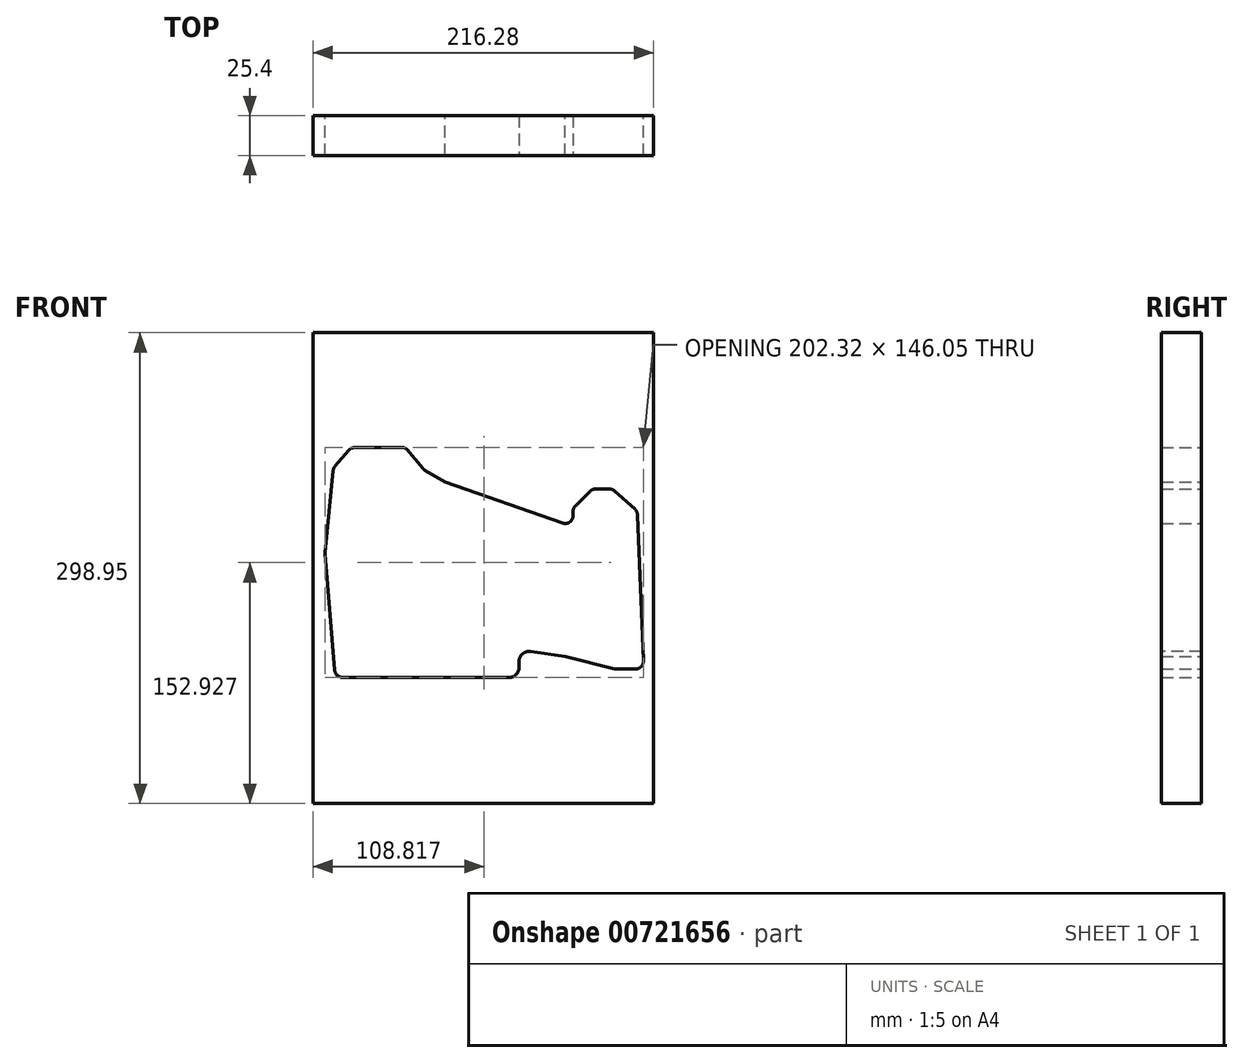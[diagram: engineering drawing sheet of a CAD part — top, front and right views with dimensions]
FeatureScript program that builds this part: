
annotation { "Feature Type Name" : "Feature", "Feature Type Description" : "" }
export const myFeature = defineFeature(function(context is Context, id is Id, definition is map)
    precondition{}
    {
        {
            var Q0;
            Q0=qCreatedBy(makeId("Front.planeOp"),FACE);
            var sketch = newSketch(context, id + "F0", { "sketchPlane" : qUnion([Q0])});
            skLineSegment(sketch, "E0", {"start": v(130.02, -238.75) * mm, "end": v(184.62, -238.75) * mm});
            skLineSegment(sketch, "E1", {"start": v(189.16, -236.13) * mm, "end": v(199.3, -218.55) * mm});
            skLineSegment(sketch, "E2", {"start": v(204.57, -215.98) * mm, "end": v(270.45, -225.26) * mm});
            skLineSegment(sketch, "E3", {"start": v(271, -225.37) * mm, "end": v(302.47, -233.24) * mm});
            skLineSegment(sketch, "E4", {"start": v(303.74, -233.4) * mm, "end": v(315.7, -233.4) * mm});
            skLineSegment(sketch, "E5", {"start": v(320.94, -227.94) * mm, "end": v(317.18, -135.48) * mm});
            skLineSegment(sketch, "E6", {"start": v(315.45, -131.79) * mm, "end": v(302.64, -120.31) * mm});
            skLineSegment(sketch, "E7", {"start": v(299.14, -118.98) * mm, "end": v(290.57, -118.98) * mm});
            skLineSegment(sketch, "E8", {"start": v(286.87, -120.51) * mm, "end": v(277.73, -129.65) * mm});
            skLineSegment(sketch, "E9", {"start": v(276.2, -133.35) * mm, "end": v(276.2, -160.7) * mm});
            skLineSegment(sketch, "E10", {"start": v(269.2, -165.64) * mm, "end": v(245.67, -157.25) * mm});
            skLineSegment(sketch, "E11", {"start": v(243.91, -156.95) * mm, "end": v(226.78, -156.95) * mm});
            skLineSegment(sketch, "E12", {"start": v(221.57, -152.22) * mm, "end": v(220.11, -137.37) * mm});
            skLineSegment(sketch, "E13", {"start": v(214.39, -132.66) * mm, "end": v(204.23, -133.66) * mm});
            skLineSegment(sketch, "E14", {"start": v(198.5, -128.95) * mm, "end": v(197.5, -118.56) * mm});
            skLineSegment(sketch, "E15", {"start": v(194.92, -114.55) * mm, "end": v(182.28, -107.17) * mm});
            skLineSegment(sketch, "E16", {"start": v(180.9, -106.01) * mm, "end": v(170.8, -93.97) * mm});
            skLineSegment(sketch, "E17", {"start": v(168.06, -92.7) * mm, "end": v(137.46, -92.7) * mm});
            skLineSegment(sketch, "E18", {"start": v(133.47, -94.54) * mm, "end": v(125.07, -104.4) * mm});
            skLineSegment(sketch, "E19", {"start": v(123.85, -107.27) * mm, "end": v(118.64, -159.2) * mm});
            skLineSegment(sketch, "E20", {"start": v(118.63, -160.17) * mm, "end": v(124.8, -233.94) * mm});
            skPoint(sketch, "E21.visualSharp", {"position": v(187.64, -238.75) * mm});
            skArc(sketch, "E21.filletArc", {"start": v(184.62, -238.75) * mm, "mid": v(187.24, -238.05) * mm, "end": v(189.16, -236.13) * mm});
            skPoint(sketch, "E22.visualSharp", {"position": v(125.2, -238.75) * mm});
            skArc(sketch, "E22.filletArc", {"start": v(124.8, -233.94) * mm, "mid": v(126.47, -237.36) * mm, "end": v(130.02, -238.75) * mm});
            skPoint(sketch, "E23.visualSharp", {"position": v(118.6, -159.69) * mm});
            skArc(sketch, "E23.filletArc", {"start": v(118.64, -159.2) * mm, "mid": v(118.62, -159.69) * mm, "end": v(118.63, -160.17) * mm});
            skPoint(sketch, "E24.visualSharp", {"position": v(124.01, -105.64) * mm});
            skArc(sketch, "E24.filletArc", {"start": v(125.07, -104.4) * mm, "mid": v(124.24, -105.74) * mm, "end": v(123.85, -107.27) * mm});
            skPoint(sketch, "E25.visualSharp", {"position": v(169.72, -92.7) * mm});
            skArc(sketch, "E25.filletArc", {"start": v(170.8, -93.97) * mm, "mid": v(169.57, -93.03) * mm, "end": v(168.06, -92.7) * mm});
            skPoint(sketch, "E26.visualSharp", {"position": v(181.49, -106.7) * mm});
            skArc(sketch, "E26.filletArc", {"start": v(180.9, -106.01) * mm, "mid": v(181.54, -106.65) * mm, "end": v(182.28, -107.17) * mm});
            skPoint(sketch, "E27.visualSharp", {"position": v(199.02, -134.17) * mm});
            skArc(sketch, "E27.filletArc", {"start": v(198.5, -128.95) * mm, "mid": v(200.4, -132.49) * mm, "end": v(204.23, -133.66) * mm});
            skPoint(sketch, "E28.visualSharp", {"position": v(219.6, -132.15) * mm});
            skArc(sketch, "E28.filletArc", {"start": v(220.11, -137.37) * mm, "mid": v(218.23, -133.83) * mm, "end": v(214.39, -132.66) * mm});
            skPoint(sketch, "E29.visualSharp", {"position": v(197.23, -115.9) * mm});
            skArc(sketch, "E29.filletArc", {"start": v(197.5, -118.56) * mm, "mid": v(196.69, -116.24) * mm, "end": v(194.92, -114.55) * mm});
            skPoint(sketch, "E30.visualSharp", {"position": v(222.03, -156.95) * mm});
            skArc(sketch, "E30.filletArc", {"start": v(221.57, -152.22) * mm, "mid": v(223.26, -155.6) * mm, "end": v(226.78, -156.95) * mm});
            skPoint(sketch, "E31.visualSharp", {"position": v(244.82, -156.95) * mm});
            skArc(sketch, "E31.filletArc", {"start": v(245.67, -157.25) * mm, "mid": v(244.8, -157.03) * mm, "end": v(243.91, -156.95) * mm});
            skPoint(sketch, "E32.visualSharp", {"position": v(276.2, -168.13) * mm});
            skArc(sketch, "E32.filletArc", {"start": v(269.2, -165.64) * mm, "mid": v(273.98, -164.98) * mm, "end": v(276.2, -160.7) * mm});
            skPoint(sketch, "E33.visualSharp", {"position": v(276.2, -131.18) * mm});
            skArc(sketch, "E33.filletArc", {"start": v(277.73, -129.65) * mm, "mid": v(276.6, -131.35) * mm, "end": v(276.2, -133.35) * mm});
            skPoint(sketch, "E34.visualSharp", {"position": v(288.4, -118.98) * mm});
            skArc(sketch, "E34.filletArc", {"start": v(290.57, -118.98) * mm, "mid": v(288.57, -119.38) * mm, "end": v(286.87, -120.51) * mm});
            skPoint(sketch, "E35.visualSharp", {"position": v(301.15, -118.98) * mm});
            skArc(sketch, "E35.filletArc", {"start": v(302.64, -120.31) * mm, "mid": v(301.02, -119.32) * mm, "end": v(299.14, -118.98) * mm});
            skPoint(sketch, "E36.visualSharp", {"position": v(317.1, -133.27) * mm});
            skArc(sketch, "E36.filletArc", {"start": v(317.18, -135.48) * mm, "mid": v(316.69, -133.46) * mm, "end": v(315.45, -131.79) * mm});
            skPoint(sketch, "E37.visualSharp", {"position": v(321.16, -233.4) * mm});
            skArc(sketch, "E37.filletArc", {"start": v(315.7, -233.4) * mm, "mid": v(319.48, -231.79) * mm, "end": v(320.94, -227.94) * mm});
            skPoint(sketch, "E38.visualSharp", {"position": v(303.1, -233.4) * mm});
            skArc(sketch, "E38.filletArc", {"start": v(302.47, -233.24) * mm, "mid": v(303.1, -233.36) * mm, "end": v(303.74, -233.4) * mm});
            skPoint(sketch, "E39.visualSharp", {"position": v(270.73, -225.3) * mm});
            skArc(sketch, "E39.filletArc", {"start": v(271, -225.37) * mm, "mid": v(270.73, -225.3) * mm, "end": v(270.45, -225.26) * mm});
            skPoint(sketch, "E40.visualSharp", {"position": v(201.07, -215.48) * mm});
            skArc(sketch, "E40.filletArc", {"start": v(204.57, -215.98) * mm, "mid": v(201.55, -216.46) * mm, "end": v(199.3, -218.55) * mm});
            skPoint(sketch, "E41.visualSharp", {"position": v(135.04, -92.7) * mm});
            skArc(sketch, "E41.filletArc", {"start": v(137.46, -92.7) * mm, "mid": v(135.27, -93.18) * mm, "end": v(133.47, -94.54) * mm});
            skPoint(sketch, "E42.visualSharp", {"position": v(223.3, -245.9) * mm});
            skPoint(sketch, "E43.visualSharp", {"position": v(263.76, -245.9) * mm});
            skPoint(sketch, "E44.visualSharp", {"position": v(223.3, -121.07) * mm});
            skPoint(sketch, "E45.visualSharp", {"position": v(263.76, -121.07) * mm});
            skLineSegment(sketch, "E46", {"start": v(204.57, -215.98) * mm, "end": v(223.3, -218.61) * mm});
            skLineSegment(sketch, "E47", {"start": v(270.45, -225.26) * mm, "end": v(263.76, -224.32) * mm});
            skLineSegment(sketch, "E48", {"start": v(269.2, -165.64) * mm, "end": v(263.76, -163.7) * mm});
            skPoint(sketch, "E49.endSnap0", {"position": v(223.26, -155.6) * mm});
            skLineSegment(sketch, "E50.bottom", {"start": v(110.96, -318.65) * mm, "end": v(327.24, -318.65) * mm});
            skLineSegment(sketch, "E50.top", {"start": v(110.96, -19.7) * mm, "end": v(327.24, -19.7) * mm});
            skLineSegment(sketch, "E50.left", {"start": v(110.96, -318.65) * mm, "end": v(110.96, -19.7) * mm});
            skLineSegment(sketch, "E50.right", {"start": v(327.24, -318.65) * mm, "end": v(327.24, -19.7) * mm});
            skSolve(sketch);
        }
        {
            var Q0;
            Q0 = qSketchRegion(id + "F0", true);
            extrude(context, id + "F1", {"entities" : qUnion([Q0]), "depth" : 25.4 * mm, "offsetDistance" : 25.4 * mm});
        }
        {
            var Q0;
            Q0=makeQuery(id+"F1.opExtrude","CAP_FACE",FACE,{"disambiguationData":[OSD([sQuery(id+"F0.wireOp",EDGE,"E0"),sQuery(id+"F0.wireOp",EDGE,"E1"),sQuery(id+"F0.wireOp",EDGE,"E2"),sQuery(id+"F0.wireOp",EDGE,"E3"),sQuery(id+"F0.wireOp",EDGE,"E4"),sQuery(id+"F0.wireOp",EDGE,"E5"),sQuery(id+"F0.wireOp",EDGE,"E6"),sQuery(id+"F0.wireOp",EDGE,"E7"),sQuery(id+"F0.wireOp",EDGE,"E8"),sQuery(id+"F0.wireOp",EDGE,"E9"),sQuery(id+"F0.wireOp",EDGE,"E10"),sQuery(id+"F0.wireOp",EDGE,"E11"),sQuery(id+"F0.wireOp",EDGE,"E12"),sQuery(id+"F0.wireOp",EDGE,"E13"),sQuery(id+"F0.wireOp",EDGE,"E14"),sQuery(id+"F0.wireOp",EDGE,"E15"),sQuery(id+"F0.wireOp",EDGE,"E16"),sQuery(id+"F0.wireOp",EDGE,"E17"),sQuery(id+"F0.wireOp",EDGE,"E18"),sQuery(id+"F0.wireOp",EDGE,"E19"),sQuery(id+"F0.wireOp",EDGE,"E20"),sQuery(id+"F0.wireOp",EDGE,"E21.filletArc"),sQuery(id+"F0.wireOp",EDGE,"E22.filletArc"),sQuery(id+"F0.wireOp",EDGE,"E23.filletArc"),sQuery(id+"F0.wireOp",EDGE,"E24.filletArc"),sQuery(id+"F0.wireOp",EDGE,"E25.filletArc"),sQuery(id+"F0.wireOp",EDGE,"E26.filletArc"),sQuery(id+"F0.wireOp",EDGE,"E27.filletArc"),sQuery(id+"F0.wireOp",EDGE,"E28.filletArc"),sQuery(id+"F0.wireOp",EDGE,"E29.filletArc"),sQuery(id+"F0.wireOp",EDGE,"E30.filletArc"),sQuery(id+"F0.wireOp",EDGE,"E31.filletArc"),sQuery(id+"F0.wireOp",EDGE,"E32.filletArc"),sQuery(id+"F0.wireOp",EDGE,"E33.filletArc"),sQuery(id+"F0.wireOp",EDGE,"E34.filletArc"),sQuery(id+"F0.wireOp",EDGE,"E35.filletArc"),sQuery(id+"F0.wireOp",EDGE,"E36.filletArc"),sQuery(id+"F0.wireOp",EDGE,"E37.filletArc"),sQuery(id+"F0.wireOp",EDGE,"E38.filletArc"),sQuery(id+"F0.wireOp",EDGE,"E39.filletArc"),sQuery(id+"F0.wireOp",EDGE,"E40.filletArc"),sQuery(id+"F0.wireOp",EDGE,"E41.filletArc"),sQuery(id+"F0.wireOp",EDGE,"E46"),sQuery(id+"F0.wireOp",EDGE,"E47"),sQuery(id+"F0.wireOp",EDGE,"E48"),sQuery(id+"F0.wireOp",EDGE,"E50.bottom"),sQuery(id+"F0.wireOp",EDGE,"E50.top"),sQuery(id+"F0.wireOp",EDGE,"E50.left"),sQuery(id+"F0.wireOp",EDGE,"E50.right")])],"isStart":false});
            var sketch = newSketch(context, id + "F2", { "sketchPlane" : qUnion([Q0])});
            skLineSegment(sketch, "E51", {"start": v(184.62, -238.75) * mm, "end": v(235.53, -238.75) * mm});
            skLineSegment(sketch, "E52", {"start": v(241.88, -232.4) * mm, "end": v(241.88, -228.55) * mm});
            skLineSegment(sketch, "E53", {"start": v(249.12, -222.26) * mm, "end": v(271, -225.37) * mm});
            skLineSegment(sketch, "E54", {"start": v(271, -225.37) * mm, "end": v(271, -172.68) * mm});
            skLineSegment(sketch, "E55", {"start": v(271, -172.68) * mm, "end": v(284.43, -163.98) * mm});
            skLineSegment(sketch, "E56", {"start": v(284.43, -163.98) * mm, "end": v(282.26, -145.12) * mm});
            skLineSegment(sketch, "E57", {"start": v(282.26, -145.12) * mm, "end": v(194.92, -114.55) * mm});
            skLineSegment(sketch, "E58", {"start": v(194.92, -114.55) * mm, "end": v(184.62, -238.75) * mm});
            skPoint(sketch, "E59.visualSharp", {"position": v(241.88, -238.75) * mm});
            skArc(sketch, "E59.filletArc", {"start": v(235.53, -238.75) * mm, "mid": v(240.02, -236.89) * mm, "end": v(241.88, -232.4) * mm});
            skPoint(sketch, "E60.visualSharp", {"position": v(241.88, -221.23) * mm});
            skArc(sketch, "E60.filletArc", {"start": v(249.12, -222.26) * mm, "mid": v(244.07, -223.75) * mm, "end": v(241.88, -228.55) * mm});
            skSolve(sketch);
        }
        {
            var Q0;
            Q0 = qSketchRegion(id + "F2", true);
            extrude(context, id + "F3", {"entities" : qUnion([Q0]), "operationType" : NewBodyOperationType.REMOVE, "endBound" : BoundingType.THROUGH_ALL, "oppositeDirection" : true, "depth" : 25.4 * mm, "offsetDistance" : 25.4 * mm});
        }
        {
            var Q0;
            Q0=makeQuery(id+"F3.boolean.opBoolean","INTERSECT",EDGE,{"derivedFrom":[makeQuery(id+"F1.opExtrude","SWEPT_FACE",FACE,{"disambiguationData":[OSD([sQuery(id+"F0.wireOp",EDGE,"E9")])]}),makeQuery(id+"F3.opExtrude","SWEPT_FACE",FACE,{"disambiguationData":[OSD([sQuery(id+"F2.wireOp",EDGE,"E57")])]})]});
            fillet(context, id + "F4", {"entities" : qUnion([Q0]), "radius" : 5.08 * mm, "tangentPropagation" : true, "allowEdgeOverflow" : false});
        }
    });
